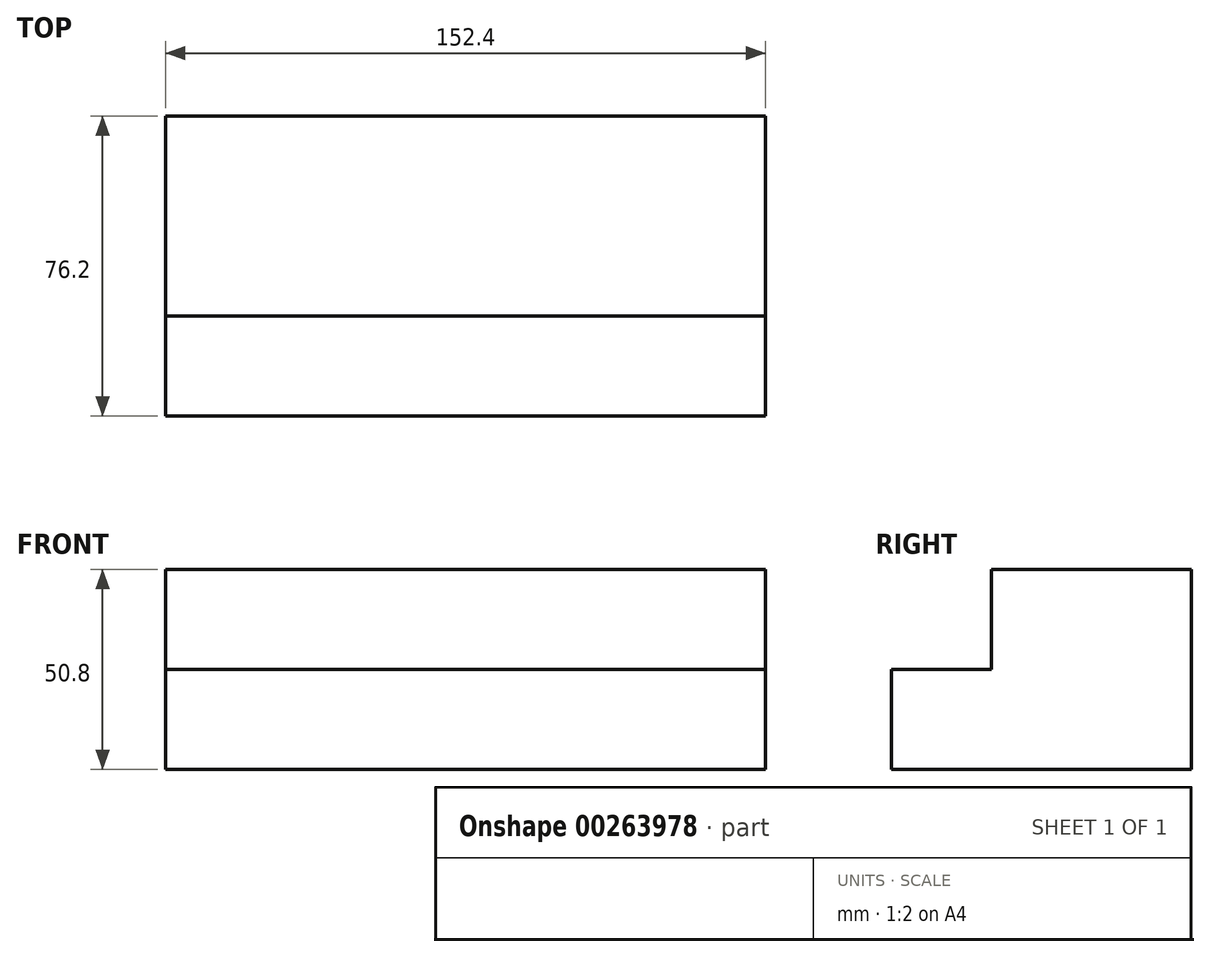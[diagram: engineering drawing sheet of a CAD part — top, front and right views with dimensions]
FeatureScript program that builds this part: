
annotation { "Feature Type Name" : "Feature", "Feature Type Description" : "" }
export const myFeature = defineFeature(function(context is Context, id is Id, definition is map)
    precondition{}
    {
        {
            var Q0;
            Q0=qCreatedBy(makeId("Right.planeOp"),FACE);
            var sketch = newSketch(context, id + "F0", { "sketchPlane" : qUnion([Q0])});
            skLineSegment(sketch, "E0", {"start": v(0, 0) * mm, "end": v(76.2, 0) * mm});
            skLineSegment(sketch, "E1", {"start": v(76.2, 0) * mm, "end": v(76.2, 50.8) * mm});
            skLineSegment(sketch, "E2", {"start": v(76.2, 50.8) * mm, "end": v(25.4, 50.8) * mm});
            skLineSegment(sketch, "E3", {"start": v(25.4, 50.8) * mm, "end": v(25.4, 25.4) * mm});
            skLineSegment(sketch, "E4", {"start": v(25.4, 25.4) * mm, "end": v(0, 25.4) * mm});
            skLineSegment(sketch, "E5", {"start": v(0, 25.4) * mm, "end": v(0, 0) * mm});
            skSolve(sketch);
        }
        {
            var Q0;
            Q0 = qSketchRegion(id + "F0", true);
            extrude(context, id + "F1", {"entities" : qUnion([Q0]), "depth" : 152.4 * mm});
        }
    });
